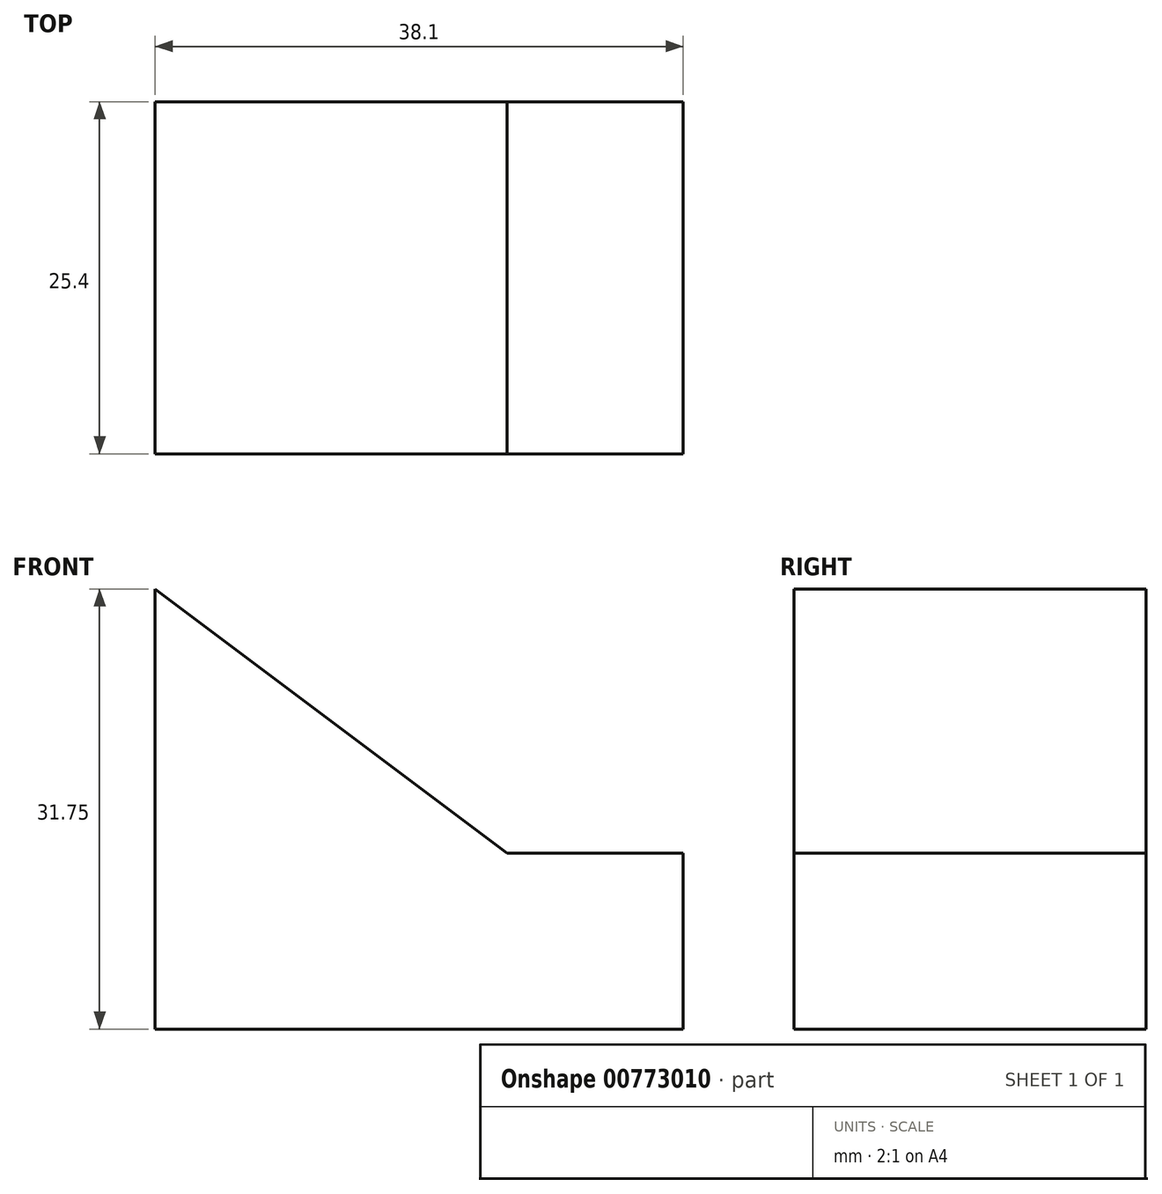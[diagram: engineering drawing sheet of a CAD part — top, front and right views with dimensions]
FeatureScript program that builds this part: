
annotation { "Feature Type Name" : "Feature", "Feature Type Description" : "" }
export const myFeature = defineFeature(function(context is Context, id is Id, definition is map)
    precondition{}
    {
        {
            var Q0;
            Q0=qCreatedBy(makeId("Front.planeOp"),FACE);
            var sketch = newSketch(context, id + "F0", { "sketchPlane" : qUnion([Q0])});
            skLineSegment(sketch, "E0", {"start": v(0, 0) * mm, "end": v(38.1, 0) * mm});
            skLineSegment(sketch, "E1", {"start": v(38.1, 0) * mm, "end": v(38.1, 12.7) * mm});
            skLineSegment(sketch, "E2", {"start": v(0, 0) * mm, "end": v(0, 31.75) * mm});
            skLineSegment(sketch, "E3", {"start": v(38.1, 12.7) * mm, "end": v(25.4, 12.7) * mm});
            skLineSegment(sketch, "E4", {"start": v(25.4, 12.7) * mm, "end": v(0, 31.75) * mm});
            skSolve(sketch);
        }
        {
            var Q0;
            Q0=makeQuery(id+"F0.imprint","IMPRINT",FACE,{"disambiguationData":[TD([[makeQuery(id+"F0.imprint","IMPRINT",EDGE,{"derivedFrom":sQuery(id+"F0.wireOp",EDGE,"E0")}),1.0]])]});
            extrude(context, id + "F1", {"entities" : qUnion([Q0]), "depth" : 25.4 * mm, "offsetDistance" : 25.4 * mm});
        }
    });
